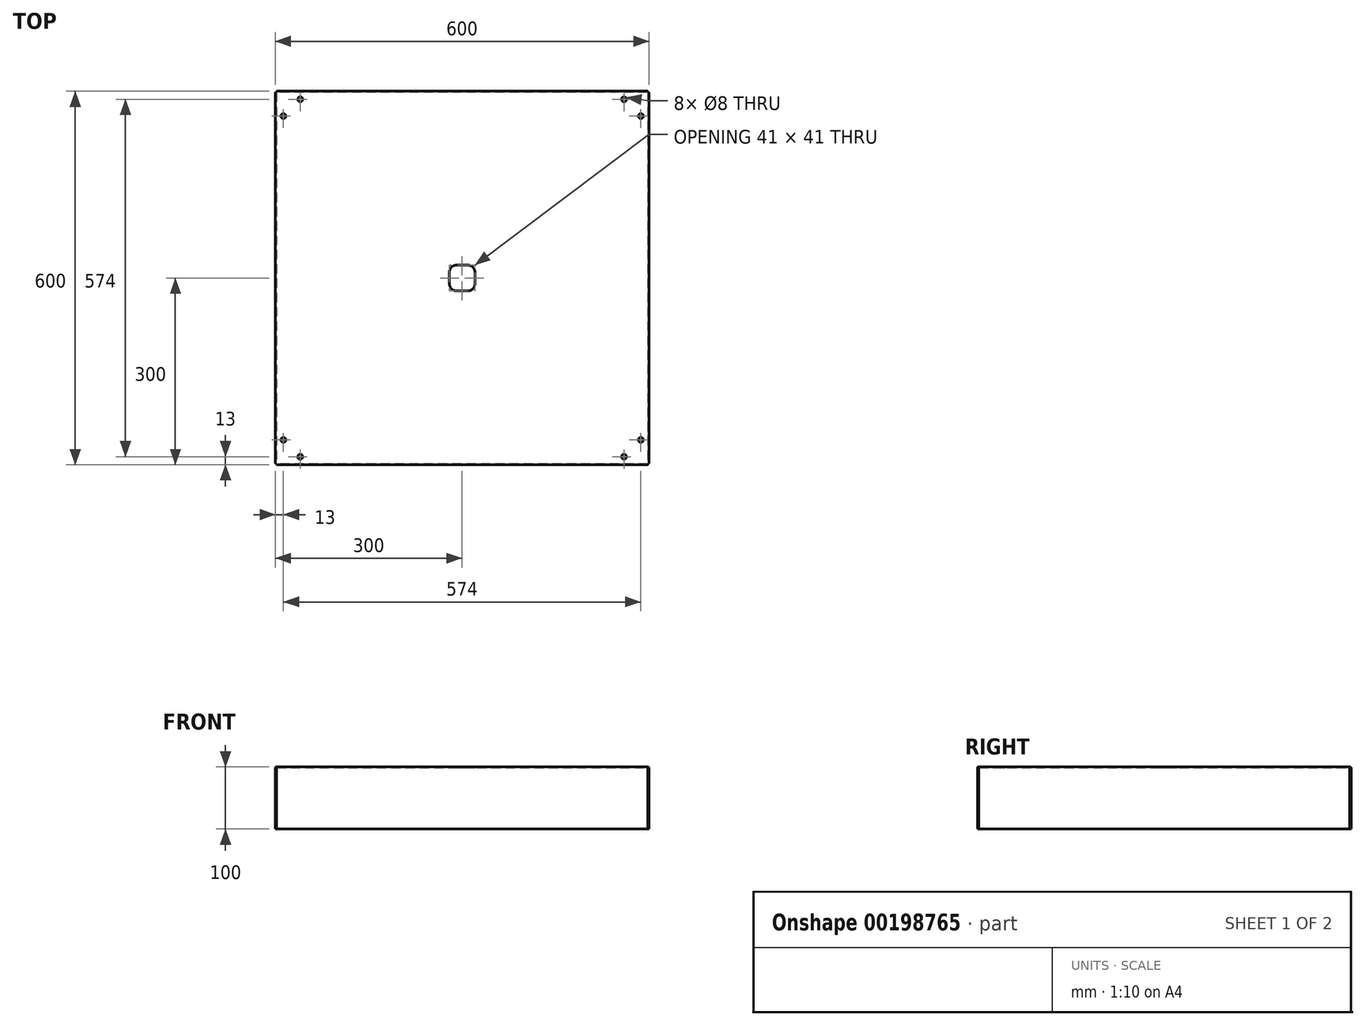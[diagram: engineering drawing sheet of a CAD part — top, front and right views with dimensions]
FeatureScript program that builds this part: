
annotation { "Feature Type Name" : "Feature", "Feature Type Description" : "" }
export const myFeature = defineFeature(function(context is Context, id is Id, definition is map)
    precondition{}
    {
        {
            var Q0;
            Q0=qCreatedBy(makeId("Top.planeOp"),FACE);
            var sketch = newSketch(context, id + "F0", { "sketchPlane" : qUnion([Q0])});
            skLineSegment(sketch, "E0.bottom", {"start": v(300, 300) * mm, "end": v(-300, 300) * mm});
            skLineSegment(sketch, "E0.top", {"start": v(300, -300) * mm, "end": v(-300, -300) * mm});
            skLineSegment(sketch, "E0.left", {"start": v(300, 300) * mm, "end": v(300, -300) * mm});
            skLineSegment(sketch, "E0.right", {"start": v(-300, 300) * mm, "end": v(-300, -300) * mm});
            skPoint(sketch, "E0.middle", {"position": v(0, 0) * mm});
            skSolve(sketch);
        }
        {
            var Q0;
            Q0=qSketchRegion(id+"F0",true);
            var Q1;
            Q1=makeQuery(id+"F0.imprint","IMPRINT",FACE,{"disambiguationData":[TD([[makeQuery(id+"F0.imprint","IMPRINT",EDGE,{"derivedFrom":sQuery(id+"F0.wireOp",EDGE,"E0.bottom")}),1.0]])]});
            extrude(context, id + "F1", {"entities" : qUnion([Q0, Q1]), "depth" : 100 * mm});
        }
        {
            var Q0;
            Q0=makeQuery(id+"F1.opExtrude","CAP_FACE",FACE,{"disambiguationData":[OSD([sQuery(id+"F0.wireOp",EDGE,"E0.bottom"),sQuery(id+"F0.wireOp",EDGE,"E0.top"),sQuery(id+"F0.wireOp",EDGE,"E0.left"),sQuery(id+"F0.wireOp",EDGE,"E0.right")])],"isStart":true});
            var sketch = newSketch(context, id + "F2", { "sketchPlane" : qUnion([Q0])});
            skLineSegment(sketch, "E1.0", {"start": v(284, -284) * mm, "end": v(284, 284) * mm});
            skLineSegment(sketch, "E1.1", {"start": v(-284, -284) * mm, "end": v(284, -284) * mm});
            skLineSegment(sketch, "E1.2", {"start": v(-284, 284) * mm, "end": v(-284, -284) * mm});
            skLineSegment(sketch, "E1.3", {"start": v(284, 284) * mm, "end": v(-284, 284) * mm});
            skSolve(sketch);
        }
        {
            var Q0;
            Q0=makeQuery(id+"F1.opExtrude","CAP_EDGE",EDGE,{"disambiguationData":[OSD([sQuery(id+"F0.wireOp",EDGE,"E0.top")])],"isStart":false});
            var Q1;
            Q1=makeQuery(id+"F1.opExtrude","SWEPT_EDGE",EDGE,{"disambiguationData":[OSD([sQuery(id+"F0.wireOp",EDGE,"E0.top"),sQuery(id+"F0.wireOp",EDGE,"E0.right")])]});
            var Q2;
            Q2=makeQuery(id+"F1.opExtrude","CAP_EDGE",EDGE,{"disambiguationData":[OSD([sQuery(id+"F0.wireOp",EDGE,"E0.right")])],"isStart":false});
            var Q3;
            Q3=makeQuery(id+"F1.opExtrude","SWEPT_EDGE",EDGE,{"disambiguationData":[OSD([sQuery(id+"F0.wireOp",EDGE,"E0.top"),sQuery(id+"F0.wireOp",EDGE,"E0.left")])]});
            var Q4;
            Q4=makeQuery(id+"F1.opExtrude","SWEPT_EDGE",EDGE,{"disambiguationData":[OSD([sQuery(id+"F0.wireOp",EDGE,"E0.bottom"),sQuery(id+"F0.wireOp",EDGE,"E0.right")])]});
            var Q5;
            Q5=makeQuery(id+"F1.opExtrude","CAP_EDGE",EDGE,{"disambiguationData":[OSD([sQuery(id+"F0.wireOp",EDGE,"E0.left")])],"isStart":false});
            var Q6;
            Q6=makeQuery(id+"F1.opExtrude","CAP_EDGE",EDGE,{"disambiguationData":[OSD([sQuery(id+"F0.wireOp",EDGE,"E0.bottom")])],"isStart":false});
            var Q7;
            Q7=makeQuery(id+"F1.opExtrude","SWEPT_EDGE",EDGE,{"disambiguationData":[OSD([sQuery(id+"F0.wireOp",EDGE,"E0.bottom"),sQuery(id+"F0.wireOp",EDGE,"E0.left")])]});
            fillet(context, id + "F3", {"entities" : qUnion([Q0, Q1, Q2, Q3, Q4, Q5, Q6, Q7]), "radius" : 2 * mm, "tangentPropagation" : true, "allowEdgeOverflow" : false});
        }
        {
            var Q0;
            {var subQ0=makeQuery(id+"F1.opExtrude","CAP_FACE",FACE,{"disambiguationData":[OSD([sQuery(id+"F0.wireOp",EDGE,"E0.bottom"),sQuery(id+"F0.wireOp",EDGE,"E0.top"),sQuery(id+"F0.wireOp",EDGE,"E0.left"),sQuery(id+"F0.wireOp",EDGE,"E0.right")])],"isStart":true});Q0=makeQuery(id+"FQFtTwVdiUHZbcw_1.opSplitFace","SPLIT",FACE,{"disambiguationData":[TD([[makeQuery(id+"FQFtTwVdiUHZbcw_1.opSplitFace","IMPRINT_ON_FACE",EDGE,{"derivedFrom":[subQ0,sQuery(id+"F2.wireOp",EDGE,"E1.0")]}),-1.0]])],"derivedFrom":subQ0});}
            shell(context, id + "F4", {"entities" : qUnion([Q0]), "thickness" : 1.6 * mm});
        }
        {
            var Q0;
            Q0=makeQuery(id+"F1.opExtrude","CAP_FACE",FACE,{"disambiguationData":[OSD([sQuery(id+"F0.wireOp",EDGE,"E0.bottom"),sQuery(id+"F0.wireOp",EDGE,"E0.top"),sQuery(id+"F0.wireOp",EDGE,"E0.left"),sQuery(id+"F0.wireOp",EDGE,"E0.right")])],"isStart":false});
            var sketch = newSketch(context, id + "F5", { "sketchPlane" : qUnion([Q0])});
            skLineSegment(sketch, "E2", {"start": v(298, 298) * mm, "end": v(300.05, 298) * mm});
            skArc(sketch, "E3.0", {"start": v(298, 300) * mm, "mid": v(299.41, 299.41) * mm, "end": v(300, 298) * mm});
            skLineSegment(sketch, "E4", {"start": v(298, 300) * mm, "end": v(298, 298) * mm});
            skLineSegment(sketch, "E5", {"start": v(0, 0) * mm, "end": v(298, 0) * mm, "construction": true});
            skLineSegment(sketch, "E6", {"start": v(0, 0) * mm, "end": v(0, 298) * mm, "construction": true});
            skLineSegment(sketch, "E7.MirrorCS", {"start": v(298, -300) * mm, "end": v(298, -298) * mm});
            skLineSegment(sketch, "E8.MirrorCS", {"start": v(298, -298) * mm, "end": v(300.05, -298) * mm});
            skArc(sketch, "E9.MirrorCS", {"start": v(298, -300) * mm, "mid": v(299.41, -299.41) * mm, "end": v(300, -298) * mm});
            skLineSegment(sketch, "E10.MirrorCS", {"start": v(-298, 298) * mm, "end": v(-300.05, 298) * mm});
            skArc(sketch, "E11.MirrorCS", {"start": v(-298, 300) * mm, "mid": v(-299.41, 299.41) * mm, "end": v(-300, 298) * mm});
            skLineSegment(sketch, "E12.MirrorCS", {"start": v(-298, 300) * mm, "end": v(-298, 298) * mm});
            skLineSegment(sketch, "E13.MirrorCS", {"start": v(-298, -300) * mm, "end": v(-298, -298) * mm});
            skLineSegment(sketch, "E14.MirrorCS", {"start": v(-298, -298) * mm, "end": v(-300.05, -298) * mm});
            skArc(sketch, "E15.MirrorCS", {"start": v(-298, -300) * mm, "mid": v(-299.41, -299.41) * mm, "end": v(-300, -298) * mm});
            skSolve(sketch);
        }
        {
            var Q0;
            Q0=qSketchRegion(id+"F5",true);
            extrude(context, id + "F6", {"entities" : qUnion([Q0]), "operationType" : NewBodyOperationType.REMOVE, "endBound" : BoundingType.THROUGH_ALL, "oppositeDirection" : true, "depth" : 25 * mm});
        }
        {
            var Q0;
            Q0=makeQuery(id+"F1.opExtrude","CAP_FACE",FACE,{"disambiguationData":[OSD([sQuery(id+"F0.wireOp",EDGE,"E0.bottom"),sQuery(id+"F0.wireOp",EDGE,"E0.top"),sQuery(id+"F0.wireOp",EDGE,"E0.left"),sQuery(id+"F0.wireOp",EDGE,"E0.right")])],"isStart":false});
            var sketch = newSketch(context, id + "F7", { "sketchPlane" : qUnion([Q0])});
            skLineSegment(sketch, "E16.bottom", {"start": v(-9.5, -20.5) * mm, "end": v(9.5, -20.5) * mm});
            skLineSegment(sketch, "E16.top", {"start": v(-9.5, 20.5) * mm, "end": v(9.5, 20.5) * mm});
            skLineSegment(sketch, "E16.left", {"start": v(-20.5, -9.5) * mm, "end": v(-20.5, 9.5) * mm});
            skLineSegment(sketch, "E16.right", {"start": v(20.5, -9.5) * mm, "end": v(20.5, 9.5) * mm});
            skPoint(sketch, "E16.middle", {"position": v(0, 0) * mm});
            skPoint(sketch, "E17.visualSharp", {"position": v(20.5, -20.5) * mm});
            skArc(sketch, "E17.filletArc", {"start": v(9.5, -20.5) * mm, "mid": v(17.28, -17.28) * mm, "end": v(20.5, -9.5) * mm});
            skPoint(sketch, "E18.visualSharp", {"position": v(-20.5, -20.5) * mm});
            skArc(sketch, "E18.filletArc", {"start": v(-20.5, -9.5) * mm, "mid": v(-17.28, -17.28) * mm, "end": v(-9.5, -20.5) * mm});
            skPoint(sketch, "E19.visualSharp", {"position": v(-20.5, 20.5) * mm});
            skArc(sketch, "E19.filletArc", {"start": v(-9.5, 20.5) * mm, "mid": v(-17.28, 17.28) * mm, "end": v(-20.5, 9.5) * mm});
            skPoint(sketch, "E20.visualSharp", {"position": v(20.5, 20.5) * mm});
            skArc(sketch, "E20.filletArc", {"start": v(20.5, 9.5) * mm, "mid": v(17.28, 17.28) * mm, "end": v(9.5, 20.5) * mm});
            skSolve(sketch);
        }
        {
            var Q0;
            Q0=qSketchRegion(id+"F7",true);
            extrude(context, id + "F8", {"entities" : qUnion([Q0]), "operationType" : NewBodyOperationType.REMOVE, "endBound" : BoundingType.THROUGH_ALL, "oppositeDirection" : true, "depth" : 25 * mm});
        }
        {
            var Q0;
            Q0=makeQuery(id+"F1.opExtrude","CAP_FACE",FACE,{"disambiguationData":[OSD([sQuery(id+"F0.wireOp",EDGE,"E0.bottom"),sQuery(id+"F0.wireOp",EDGE,"E0.top"),sQuery(id+"F0.wireOp",EDGE,"E0.left"),sQuery(id+"F0.wireOp",EDGE,"E0.right")])],"isStart":false});
            var sketch = newSketch(context, id + "F9", { "sketchPlane" : qUnion([Q0])});
            skLineSegment(sketch, "E21.0", {"start": v(-298, 287) * mm, "end": v(298, 287) * mm, "construction": true});
            skLineSegment(sketch, "E22", {"start": v(0, 0) * mm, "end": v(0, 287) * mm, "construction": true});
            skCircle(sketch, "E23", {"center": v(260, 287) * mm, "radius": 4 * mm});
            skCircle(sketch, "E24.MirrorC", {"center": v(-260, 287) * mm, "radius": 4 * mm});
            skCircle(sketch, "E25.1.0", {"center": v(-287, -260) * mm, "radius": 4 * mm});
            skCircle(sketch, "E25.1.1", {"center": v(-287, 260) * mm, "radius": 4 * mm});
            skCircle(sketch, "E25.2.0", {"center": v(260, -287) * mm, "radius": 4 * mm});
            skCircle(sketch, "E25.2.1", {"center": v(-260, -287) * mm, "radius": 4 * mm});
            skCircle(sketch, "E25.3.0", {"center": v(287, 260) * mm, "radius": 4 * mm});
            skCircle(sketch, "E25.3.1", {"center": v(287, -260) * mm, "radius": 4 * mm});
            skPoint(sketch, "E25.center", {"position": v(0, 0) * mm});
            skSolve(sketch);
        }
        {
            var Q0;
            Q0=qSketchRegion(id+"F9",true);
            extrude(context, id + "F10", {"entities" : qUnion([Q0]), "operationType" : NewBodyOperationType.REMOVE, "endBound" : BoundingType.THROUGH_ALL, "oppositeDirection" : true, "depth" : 25 * mm});
        }
    });
